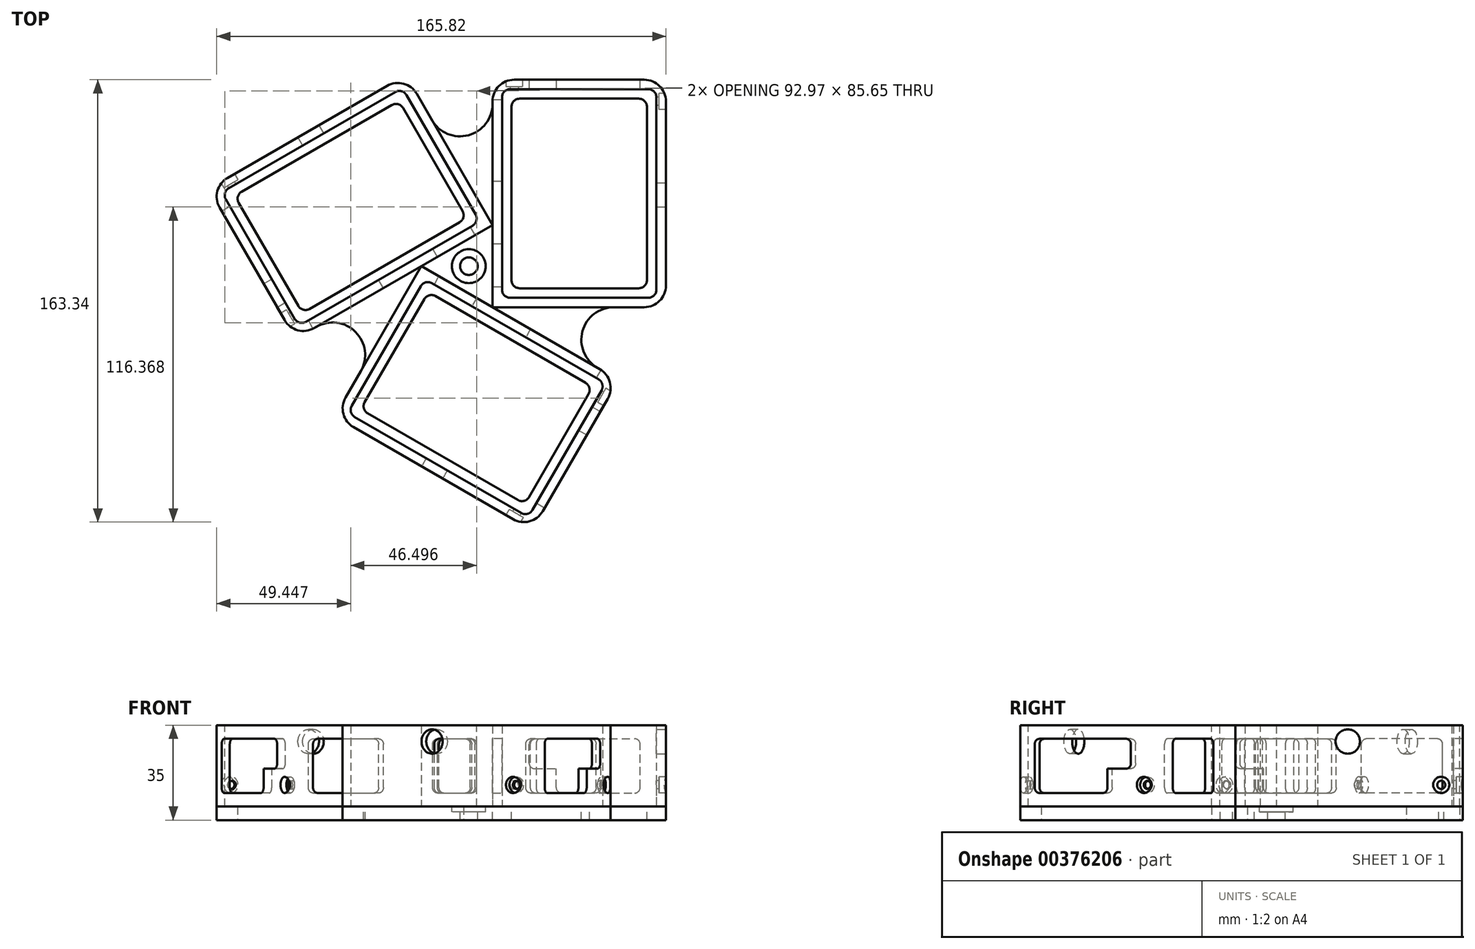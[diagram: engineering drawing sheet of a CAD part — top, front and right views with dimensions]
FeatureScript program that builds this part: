
annotation { "Feature Type Name" : "Feature", "Feature Type Description" : "" }
export const myFeature = defineFeature(function(context is Context, id is Id, definition is map)
    precondition{}
    {
        {
            var Q0;
            Q0=qCreatedBy(makeId("Top.planeOp"),FACE);
            var sketch = newSketch(context, id + "F0", { "sketchPlane" : qUnion([Q0])});
            skCircle(sketch, "E0.cCircle", {"center": v(0, 0) * mm, "radius": 8.75 * mm, "construction": true});
            skLineSegment(sketch, "E1.bottom", {"start": v(12.25, 65.34) * mm, "end": v(69.25, 65.34) * mm});
            skLineSegment(sketch, "E1.top", {"start": v(12.25, -11.66) * mm, "end": v(69.25, -11.66) * mm});
            skLineSegment(sketch, "E1.left", {"start": v(12.25, 65.34) * mm, "end": v(12.25, -11.66) * mm});
            skLineSegment(sketch, "E1.right", {"start": v(69.25, 65.34) * mm, "end": v(69.25, -11.66) * mm});
            skLineSegment(sketch, "E2.0", {"start": v(8.75, 68.84) * mm, "end": v(72.75, 68.84) * mm});
            skLineSegment(sketch, "E2.1", {"start": v(8.75, 68.84) * mm, "end": v(8.75, -15.16) * mm});
            skLineSegment(sketch, "E2.2", {"start": v(8.75, -15.16) * mm, "end": v(72.75, -15.16) * mm});
            skLineSegment(sketch, "E2.3", {"start": v(72.75, 68.84) * mm, "end": v(72.75, -15.16) * mm});
            skLineSegment(sketch, "E3.bottom", {"start": v(-44.72, -54.14) * mm, "end": v(-16.22, -4.78) * mm});
            skLineSegment(sketch, "E3.top", {"start": v(21.97, -92.64) * mm, "end": v(50.47, -43.28) * mm});
            skLineSegment(sketch, "E3.left", {"start": v(-44.72, -54.14) * mm, "end": v(21.97, -92.64) * mm});
            skLineSegment(sketch, "E3.right", {"start": v(-16.22, -4.78) * mm, "end": v(50.47, -43.28) * mm});
            skLineSegment(sketch, "E4.0", {"start": v(-49.5, -55.43) * mm, "end": v(-17.5, 0) * mm});
            skLineSegment(sketch, "E4.1", {"start": v(-49.5, -55.43) * mm, "end": v(23.25, -97.43) * mm});
            skLineSegment(sketch, "E4.2", {"start": v(23.25, -97.43) * mm, "end": v(55.25, -42) * mm});
            skLineSegment(sketch, "E4.3", {"start": v(-17.5, 0) * mm, "end": v(55.25, -42) * mm});
            skLineSegment(sketch, "E5.0", {"start": v(-64, -26.84) * mm, "end": v(-96, 28.58) * mm});
            skLineSegment(sketch, "E5.1", {"start": v(-64, -26.84) * mm, "end": v(8.75, 15.16) * mm});
            skLineSegment(sketch, "E5.2", {"start": v(8.75, 15.16) * mm, "end": v(-23.25, 70.58) * mm});
            skLineSegment(sketch, "E5.3", {"start": v(-96, 28.58) * mm, "end": v(-23.25, 70.58) * mm});
            skLineSegment(sketch, "E6.0", {"start": v(15.75, 61.84) * mm, "end": v(15.75, -8.16) * mm});
            skLineSegment(sketch, "E6.1", {"start": v(15.75, 61.84) * mm, "end": v(65.75, 61.84) * mm});
            skLineSegment(sketch, "E6.2", {"start": v(65.75, 61.84) * mm, "end": v(65.75, -8.16) * mm});
            skLineSegment(sketch, "E6.3", {"start": v(15.75, -8.16) * mm, "end": v(65.75, -8.16) * mm});
            skLineSegment(sketch, "E7.0", {"start": v(-39.94, -52.86) * mm, "end": v(-14.94, -9.56) * mm});
            skLineSegment(sketch, "E7.1", {"start": v(-39.94, -52.86) * mm, "end": v(20.68, -87.86) * mm});
            skLineSegment(sketch, "E7.2", {"start": v(20.68, -87.86) * mm, "end": v(45.68, -44.56) * mm});
            skLineSegment(sketch, "E7.3", {"start": v(-14.94, -9.56) * mm, "end": v(45.68, -44.56) * mm});
            skCircle(sketch, "E8", {"center": v(0, 0) * mm, "radius": 6.25 * mm});
            skCircle(sketch, "E9", {"center": v(0, 0) * mm, "radius": 3.25 * mm});
            skLineSegment(sketch, "E10.0", {"start": v(-91.22, 27.3) * mm, "end": v(-24.53, 65.8) * mm});
            skLineSegment(sketch, "E10.1", {"start": v(-62.72, -22.06) * mm, "end": v(-91.22, 27.3) * mm});
            skLineSegment(sketch, "E10.2", {"start": v(-62.72, -22.06) * mm, "end": v(3.97, 16.44) * mm});
            skLineSegment(sketch, "E10.3", {"start": v(3.97, 16.44) * mm, "end": v(-24.53, 65.8) * mm});
            skLineSegment(sketch, "E11.0", {"start": v(-86.43, 26.02) * mm, "end": v(-25.81, 61.02) * mm});
            skLineSegment(sketch, "E11.1", {"start": v(-61.43, -17.28) * mm, "end": v(-86.43, 26.02) * mm});
            skLineSegment(sketch, "E11.2", {"start": v(-61.43, -17.28) * mm, "end": v(-0.81, 17.72) * mm});
            skLineSegment(sketch, "E11.3", {"start": v(-0.81, 17.72) * mm, "end": v(-25.81, 61.02) * mm});
            skSolve(sketch);
        }
        {
            var Q0;
            Q0=makeQuery(id+"F0.imprint","IMPRINT",FACE,{"disambiguationData":[TD([[makeQuery(id+"F0.imprint","IMPRINT",EDGE,{"derivedFrom":sQuery(id+"F0.wireOp",EDGE,"E1.bottom")}),1.0]])]});
            var Q1;
            Q1=makeQuery(id+"F0.imprint","IMPRINT",FACE,{"disambiguationData":[TD([[makeQuery(id+"F0.imprint","IMPRINT",EDGE,{"derivedFrom":sQuery(id+"F0.wireOp",EDGE,"E1.bottom")}),-1.0]])]});
            var Q2;
            Q2=makeQuery(id+"F0.imprint","IMPRINT",FACE,{"disambiguationData":[TD([[makeQuery(id+"F0.imprint","IMPRINT",EDGE,{"derivedFrom":sQuery(id+"F0.wireOp",EDGE,"fd176c51-96d4-47cc-b5ac-51faa9285e0e.bottom")}),1.0]])]});
            var Q3;
            Q3=makeQuery(id+"F0.imprint","IMPRINT",FACE,{"disambiguationData":[TD([[makeQuery(id+"F0.imprint","IMPRINT",EDGE,{"derivedFrom":sQuery(id+"F0.wireOp",EDGE,"fd176c51-96d4-47cc-b5ac-51faa9285e0e.bottom")}),-1.0]])]});
            var Q4;
            {var subQ3=sQuery(id+"F0.wireOp",EDGE,"Trs6sdYQ-4i84-jObw-JwDY-IEx57dNpuPkq");Q4=makeQuery(id+"F0.imprint","IMPRINT",FACE,{"disambiguationData":[TD([[makeQuery(id+"F0.imprint","IMPRINT",EDGE,{"derivedFrom":subQ3}),1.0]])]});}
            var Q5;
            {var subQ3=sQuery(id+"F0.wireOp",EDGE,"4pj0R1mP-d1zE-uwOY-dOB5-XZU3ohouCTzi");Q5=makeQuery(id+"F0.imprint","IMPRINT",FACE,{"disambiguationData":[TD([[makeQuery(id+"F0.imprint","IMPRINT",EDGE,{"derivedFrom":subQ3}),1.0]])]});}
            var Q6;
            {var subQ0=sQuery(id+"F0.wireOp",EDGE,"E0.0");Q6=makeQuery(id+"F0.imprint","IMPRINT",FACE,{"disambiguationData":[TD([[makeQuery(id+"F0.imprint","IMPRINT",EDGE,{"derivedFrom":subQ0}),1.0]])]});}
            var Q7;
            {var subQ0=sQuery(id+"F0.wireOp",EDGE,"E5.2");Q7=makeQuery(id+"F0.imprint","IMPRINT",FACE,{"disambiguationData":[TD([[makeQuery(id+"F0.imprint","IMPRINT",EDGE,{"derivedFrom":subQ0}),-1.0]])]});}
            var Q8;
            {var subQ0=sQuery(id+"F0.wireOp",EDGE,"E2.2");Q8=makeQuery(id+"F0.imprint","IMPRINT",FACE,{"disambiguationData":[TD([[makeQuery(id+"F0.imprint","IMPRINT",EDGE,{"derivedFrom":subQ0}),-1.0]])]});}
            var Q9;
            {var subQ0=sQuery(id+"F0.wireOp",EDGE,"E0.0");Q9=makeQuery(id+"F0.imprint","IMPRINT",FACE,{"disambiguationData":[TD([[makeQuery(id+"F0.imprint","IMPRINT",EDGE,{"derivedFrom":subQ0}),-1.0]])]});}
            var Q10;
            Q10=makeQuery(id+"F0.imprint","IMPRINT",FACE,{"disambiguationData":[TD([[makeQuery(id+"F0.imprint","IMPRINT",EDGE,{"derivedFrom":sQuery(id+"F0.wireOp",EDGE,"E3.bottom")}),-1.0]])]});
            var Q11;
            Q11=makeQuery(id+"F0.imprint","IMPRINT",FACE,{"disambiguationData":[TD([[makeQuery(id+"F0.imprint","IMPRINT",EDGE,{"derivedFrom":sQuery(id+"F0.wireOp",EDGE,"E3.bottom")}),1.0]])]});
            var Q12;
            {var subQ3=sQuery(id+"F0.wireOp",EDGE,"SlVnMKC8-odKH-QQK0-Q7Xs-DCQOM6dgWicU");Q12=makeQuery(id+"F0.imprint","IMPRINT",FACE,{"disambiguationData":[TD([[makeQuery(id+"F0.imprint","IMPRINT",EDGE,{"derivedFrom":subQ3}),1.0]])]});}
            var Q13;
            Q13=makeQuery(id+"F0.imprint","IMPRINT",FACE,{"disambiguationData":[TD([[makeQuery(id+"F0.imprint","IMPRINT",EDGE,{"derivedFrom":sQuery(id+"F0.wireOp",EDGE,"E8")}),-1.0]])]});
            var Q14;
            Q14=makeQuery(id+"F0.imprint","IMPRINT",FACE,{"disambiguationData":[TD([[makeQuery(id+"F0.imprint","IMPRINT",EDGE,{"derivedFrom":sQuery(id+"F0.wireOp",EDGE,"E8")}),1.0]])]});
            var Q15;
            {var subQ5=sQuery(id+"F0.wireOp",EDGE,"E5.0");Q15=makeQuery(id+"F0.imprint","IMPRINT",FACE,{"disambiguationData":[TD([[makeQuery(id+"F0.imprint","IMPRINT",EDGE,{"derivedFrom":subQ5}),-1.0]])]});}
            var Q16;
            Q16=makeQuery(id+"F0.imprint","IMPRINT",FACE,{"disambiguationData":[TD([[makeQuery(id+"F0.imprint","IMPRINT",EDGE,{"derivedFrom":sQuery(id+"F0.wireOp",EDGE,"E10.0")}),-1.0]])]});
            extrude(context, id + "F1", {"entities" : qUnion([Q0, Q1, Q2, Q3, Q4, Q5, Q6, Q7, Q8, Q9, Q10, Q11, Q12, Q13, Q14, Q15, Q16]), "oppositeDirection" : true, "depth" : 5 * mm, "offsetDistance" : 25 * mm});
        }
        {
            var Q0;
            Q0=makeQuery(id+"F0.imprint","IMPRINT",FACE,{"disambiguationData":[TD([[makeQuery(id+"F0.imprint","IMPRINT",EDGE,{"derivedFrom":sQuery(id+"F0.wireOp",EDGE,"E8")}),1.0]])]});
            extrude(context, id + "F2", {"entities" : qUnion([Q0]), "operationType" : NewBodyOperationType.REMOVE, "oppositeDirection" : true, "depth" : 2 * mm, "offsetDistance" : 25 * mm});
        }
        {
            var Q0;
            Q0=makeQuery(id+"F0.imprint","IMPRINT",FACE,{"disambiguationData":[TD([[makeQuery(id+"F0.imprint","IMPRINT",EDGE,{"derivedFrom":sQuery(id+"F0.wireOp",EDGE,"E1.bottom")}),-1.0]])]});
            var Q1;
            Q1=makeQuery(id+"F0.imprint","IMPRINT",FACE,{"disambiguationData":[TD([[makeQuery(id+"F0.imprint","IMPRINT",EDGE,{"derivedFrom":sQuery(id+"F0.wireOp",EDGE,"fd176c51-96d4-47cc-b5ac-51faa9285e0e.bottom")}),-1.0]])]});
            var Q2;
            Q2=makeQuery(id+"F0.imprint","IMPRINT",FACE,{"disambiguationData":[TD([[makeQuery(id+"F0.imprint","IMPRINT",EDGE,{"derivedFrom":sQuery(id+"F0.wireOp",EDGE,"E3.bottom")}),-1.0]])]});
            extrude(context, id + "F3", {"entities" : qUnion([Q0, Q1, Q2]), "operationType" : NewBodyOperationType.REMOVE, "depth" : 3 * mm, "offsetDistance" : 25 * mm});
        }
        {
            var Q0;
            Q0=makeQuery(id+"F0.imprint","IMPRINT",FACE,{"disambiguationData":[TD([[makeQuery(id+"F0.imprint","IMPRINT",EDGE,{"derivedFrom":sQuery(id+"F0.wireOp",EDGE,"E1.bottom")}),1.0]])]});
            var Q1;
            Q1=makeQuery(id+"F0.imprint","IMPRINT",FACE,{"disambiguationData":[TD([[makeQuery(id+"F0.imprint","IMPRINT",EDGE,{"derivedFrom":sQuery(id+"F0.wireOp",EDGE,"E3.bottom")}),1.0]])]});
            var Q2;
            Q2=makeQuery(id+"F0.imprint","IMPRINT",FACE,{"disambiguationData":[TD([[makeQuery(id+"F0.imprint","IMPRINT",EDGE,{"derivedFrom":sQuery(id+"F0.wireOp",EDGE,"fd176c51-96d4-47cc-b5ac-51faa9285e0e.bottom")}),1.0]])]});
            var Q3;
            {var subQ5=sQuery(id+"F0.wireOp",EDGE,"E5.0");Q3=makeQuery(id+"F0.imprint","IMPRINT",FACE,{"disambiguationData":[TD([[makeQuery(id+"F0.imprint","IMPRINT",EDGE,{"derivedFrom":subQ5}),-1.0]])]});}
            extrude(context, id + "F4", {"entities" : qUnion([Q0, Q1, Q2, Q3]), "depth" : 30 * mm, "offsetDistance" : 25 * mm});
        }
        {
            var Q0;
            Q0=makeQuery(id+"F4.opExtrude","CAP_FACE",FACE,{"disambiguationData":[OSD([sQuery(id+"F0.wireOp",EDGE,"fd176c51-96d4-47cc-b5ac-51faa9285e0e.bottom"),sQuery(id+"F0.wireOp",EDGE,"fd176c51-96d4-47cc-b5ac-51faa9285e0e.top"),sQuery(id+"F0.wireOp",EDGE,"fd176c51-96d4-47cc-b5ac-51faa9285e0e.left"),sQuery(id+"F0.wireOp",EDGE,"fd176c51-96d4-47cc-b5ac-51faa9285e0e.right"),sQuery(id+"F0.wireOp",EDGE,"E5.0"),sQuery(id+"F0.wireOp",EDGE,"E5.1"),sQuery(id+"F0.wireOp",EDGE,"E5.2"),sQuery(id+"F0.wireOp",EDGE,"E5.3")])],"isStart":false});
            var sketch = newSketch(context, id + "F5", { "sketchPlane" : qUnion([Q0])});
            skLineSegment(sketch, "E12", {"start": v(-91.25, 20.35) * mm, "end": v(-88.22, 22.1) * mm});
            skLineSegment(sketch, "E13", {"start": v(-88.22, 22.1) * mm, "end": v(-72.72, -4.74) * mm});
            skLineSegment(sketch, "E14", {"start": v(-72.72, -4.74) * mm, "end": v(-75.75, -6.5) * mm});
            skLineSegment(sketch, "E15", {"start": v(-75.75, -6.5) * mm, "end": v(-91.25, 20.35) * mm});
            skLineSegment(sketch, "E16", {"start": v(-75.75, -6.5) * mm, "end": v(-70.75, -15.15) * mm});
            skLineSegment(sketch, "E17", {"start": v(-70.75, -15.15) * mm, "end": v(-67.72, -13.4) * mm});
            skLineSegment(sketch, "E18", {"start": v(-67.72, -13.4) * mm, "end": v(-72.72, -4.74) * mm});
            skLineSegment(sketch, "E19", {"start": v(-59.25, -20.06) * mm, "end": v(-57.5, -23.1) * mm});
            skLineSegment(sketch, "E20", {"start": v(-57.5, -23.1) * mm, "end": v(-31.52, -8.1) * mm});
            skLineSegment(sketch, "E21", {"start": v(-31.52, -8.1) * mm, "end": v(-33.27, -5.06) * mm});
            skLineSegment(sketch, "E22", {"start": v(-33.27, -5.06) * mm, "end": v(-59.25, -20.06) * mm});
            skLineSegment(sketch, "E23", {"start": v(-11.6, 3.4) * mm, "end": v(-13.35, 6.44) * mm});
            skLineSegment(sketch, "E24", {"start": v(-13.35, 6.44) * mm, "end": v(0.5, 14.44) * mm});
            skLineSegment(sketch, "E25", {"start": v(0.5, 14.44) * mm, "end": v(2.25, 11.4) * mm});
            skLineSegment(sketch, "E26", {"start": v(2.25, 11.4) * mm, "end": v(-11.6, 3.4) * mm});
            skSolve(sketch);
        }
        {
            var Q0;
            Q0=makeQuery(id+"F4.opExtrude","CAP_FACE",FACE,{"disambiguationData":[OSD([sQuery(id+"F0.wireOp",EDGE,"E3.bottom"),sQuery(id+"F0.wireOp",EDGE,"E3.top"),sQuery(id+"F0.wireOp",EDGE,"E3.left"),sQuery(id+"F0.wireOp",EDGE,"E3.right"),sQuery(id+"F0.wireOp",EDGE,"E4.0"),sQuery(id+"F0.wireOp",EDGE,"E4.1"),sQuery(id+"F0.wireOp",EDGE,"E4.2"),sQuery(id+"F0.wireOp",EDGE,"E4.3")])],"isStart":false});
            var sketch = newSketch(context, id + "F6", { "sketchPlane" : qUnion([Q0])});
            skLineSegment(sketch, "E27", {"start": v(24.97, -87.45) * mm, "end": v(28, -89.2) * mm});
            skLineSegment(sketch, "E28", {"start": v(28, -89.2) * mm, "end": v(43.5, -62.35) * mm});
            skLineSegment(sketch, "E29", {"start": v(43.5, -62.35) * mm, "end": v(40.47, -60.6) * mm});
            skLineSegment(sketch, "E30", {"start": v(40.47, -60.6) * mm, "end": v(24.97, -87.45) * mm});
            skLineSegment(sketch, "E31", {"start": v(40.47, -60.6) * mm, "end": v(45.47, -51.94) * mm});
            skLineSegment(sketch, "E32", {"start": v(45.47, -51.94) * mm, "end": v(48.5, -53.7) * mm});
            skLineSegment(sketch, "E33", {"start": v(48.5, -53.7) * mm, "end": v(43.5, -62.35) * mm});
            skLineSegment(sketch, "E34", {"start": v(48.75, -38.25) * mm, "end": v(22.77, -23.25) * mm});
            skLineSegment(sketch, "E35", {"start": v(48.75, -38.25) * mm, "end": v(47, -41.28) * mm});
            skLineSegment(sketch, "E36", {"start": v(22.77, -23.25) * mm, "end": v(21.02, -26.28) * mm});
            skLineSegment(sketch, "E37", {"start": v(21.02, -26.28) * mm, "end": v(47, -41.28) * mm});
            skLineSegment(sketch, "E38", {"start": v(-12.75, -6.78) * mm, "end": v(-11, -3.75) * mm});
            skLineSegment(sketch, "E39", {"start": v(-11, -3.75) * mm, "end": v(2.85, -11.75) * mm});
            skLineSegment(sketch, "E40", {"start": v(2.85, -11.75) * mm, "end": v(1.1, -14.78) * mm});
            skLineSegment(sketch, "E41", {"start": v(1.1, -14.78) * mm, "end": v(-12.75, -6.78) * mm});
            skSolve(sketch);
        }
        {
            var Q0;
            Q0=makeQuery(id+"F4.opExtrude","CAP_FACE",FACE,{"disambiguationData":[OSD([sQuery(id+"F0.wireOp",EDGE,"E1.bottom"),sQuery(id+"F0.wireOp",EDGE,"E1.top"),sQuery(id+"F0.wireOp",EDGE,"E1.left"),sQuery(id+"F0.wireOp",EDGE,"E1.right"),sQuery(id+"F0.wireOp",EDGE,"E2.0"),sQuery(id+"F0.wireOp",EDGE,"E2.1"),sQuery(id+"F0.wireOp",EDGE,"E2.2"),sQuery(id+"F0.wireOp",EDGE,"E2.3")])],"isStart":false});
            var sketch = newSketch(context, id + "F7", { "sketchPlane" : qUnion([Q0])});
            skLineSegment(sketch, "E42", {"start": v(32.25, 68.84) * mm, "end": v(32.25, 65.34) * mm});
            skLineSegment(sketch, "E43", {"start": v(32.25, 65.34) * mm, "end": v(63.25, 65.34) * mm});
            skLineSegment(sketch, "E44", {"start": v(63.25, 65.34) * mm, "end": v(63.25, 68.84) * mm});
            skLineSegment(sketch, "E45", {"start": v(63.25, 68.84) * mm, "end": v(32.25, 68.84) * mm});
            skLineSegment(sketch, "E46", {"start": v(32.25, 68.84) * mm, "end": v(22.25, 68.84) * mm});
            skLineSegment(sketch, "E47", {"start": v(22.25, 68.84) * mm, "end": v(22.25, 65.34) * mm});
            skLineSegment(sketch, "E48", {"start": v(22.25, 65.34) * mm, "end": v(32.25, 65.34) * mm});
            skLineSegment(sketch, "E49", {"start": v(12.25, 61.34) * mm, "end": v(8.75, 61.34) * mm});
            skLineSegment(sketch, "E50", {"start": v(12.25, 31.34) * mm, "end": v(12.25, 61.34) * mm});
            skLineSegment(sketch, "E51", {"start": v(12.25, 31.34) * mm, "end": v(8.75, 31.34) * mm});
            skLineSegment(sketch, "E52", {"start": v(8.75, 31.34) * mm, "end": v(8.75, 61.34) * mm});
            skLineSegment(sketch, "E53", {"start": v(8.75, 8.34) * mm, "end": v(12.25, 8.34) * mm});
            skLineSegment(sketch, "E54", {"start": v(12.25, 8.34) * mm, "end": v(12.25, -7.66) * mm});
            skLineSegment(sketch, "E55", {"start": v(12.25, -7.66) * mm, "end": v(8.75, -7.66) * mm});
            skLineSegment(sketch, "E56", {"start": v(8.75, -7.66) * mm, "end": v(8.75, 8.34) * mm});
            skSolve(sketch);
        }
        {
            var Q0;
            Q0=makeQuery(id+"F6.imprint","IMPRINT",FACE,{"disambiguationData":[TD([[makeQuery(id+"F6.imprint","IMPRINT",EDGE,{"derivedFrom":sQuery(id+"F6.wireOp",EDGE,"E27")}),1.0]])]});
            var Q1;
            Q1=makeQuery(id+"F7.imprint","IMPRINT",FACE,{"disambiguationData":[TD([[makeQuery(id+"F7.imprint","IMPRINT",EDGE,{"derivedFrom":sQuery(id+"F7.wireOp",EDGE,"E42")}),1.0]])]});
            var Q2;
            Q2=makeQuery(id+"F5.imprint","IMPRINT",FACE,{"disambiguationData":[TD([[makeQuery(id+"F5.imprint","IMPRINT",EDGE,{"derivedFrom":sQuery(id+"F5.wireOp",EDGE,"E12")}),-1.0]])]});
            var Q3;
            Q3=makeQuery(id+"F5.imprint","IMPRINT",FACE,{"disambiguationData":[TD([[makeQuery(id+"F5.imprint","IMPRINT",EDGE,{"derivedFrom":sQuery(id+"F5.wireOp",EDGE,"E19")}),1.0]])]});
            var Q4;
            Q4=makeQuery(id+"F7.imprint","IMPRINT",FACE,{"disambiguationData":[TD([[makeQuery(id+"F7.imprint","IMPRINT",EDGE,{"derivedFrom":sQuery(id+"F7.wireOp",EDGE,"E49")}),1.0]])]});
            var Q5;
            Q5=makeQuery(id+"F6.imprint","IMPRINT",FACE,{"disambiguationData":[TD([[makeQuery(id+"F6.imprint","IMPRINT",EDGE,{"derivedFrom":sQuery(id+"F6.wireOp",EDGE,"E34")}),-1.0]])]});
            var Q6;
            Q6=makeQuery(id+"F7.imprint","IMPRINT",FACE,{"disambiguationData":[TD([[makeQuery(id+"F7.imprint","IMPRINT",EDGE,{"derivedFrom":sQuery(id+"F7.wireOp",EDGE,"E53")}),-1.0]])]});
            var Q7;
            Q7=makeQuery(id+"F5.imprint","IMPRINT",FACE,{"disambiguationData":[TD([[makeQuery(id+"F5.imprint","IMPRINT",EDGE,{"derivedFrom":sQuery(id+"F5.wireOp",EDGE,"E23")}),-1.0]])]});
            var Q8;
            Q8=makeQuery(id+"F6.imprint","IMPRINT",FACE,{"disambiguationData":[TD([[makeQuery(id+"F6.imprint","IMPRINT",EDGE,{"derivedFrom":sQuery(id+"F6.wireOp",EDGE,"E38")}),-1.0]])]});
            extrude(context, id + "F8", {"entities" : qUnion([Q0, Q1, Q2, Q3, Q4, Q5, Q6, Q7, Q8]), "operationType" : NewBodyOperationType.REMOVE, "oppositeDirection" : true, "depth" : 25 * mm, "offsetDistance" : 25 * mm, "hasSecondDirection" : true, "secondDirectionOppositeDirection" : true, "secondDirectionDepth" : 5 * mm});
        }
        {
            var Q0;
            Q0=makeQuery(id+"F5.imprint","IMPRINT",FACE,{"disambiguationData":[TD([[makeQuery(id+"F5.imprint","IMPRINT",EDGE,{"derivedFrom":sQuery(id+"F5.wireOp",EDGE,"E14")}),1.0]])]});
            var Q1;
            Q1=makeQuery(id+"F6.imprint","IMPRINT",FACE,{"disambiguationData":[TD([[makeQuery(id+"F6.imprint","IMPRINT",EDGE,{"derivedFrom":sQuery(id+"F6.wireOp",EDGE,"E29")}),-1.0]])]});
            var Q2;
            Q2=makeQuery(id+"F7.imprint","IMPRINT",FACE,{"disambiguationData":[TD([[makeQuery(id+"F7.imprint","IMPRINT",EDGE,{"derivedFrom":sQuery(id+"F7.wireOp",EDGE,"E42")}),-1.0]])]});
            extrude(context, id + "F9", {"entities" : qUnion([Q0, Q1, Q2]), "operationType" : NewBodyOperationType.REMOVE, "oppositeDirection" : true, "depth" : 16 * mm, "offsetDistance" : 25 * mm, "hasSecondDirection" : true, "secondDirectionOppositeDirection" : true, "secondDirectionDepth" : 5 * mm});
        }
        {
            var Q0;
            Q0=makeQuery(id+"F4.opExtrude","SWEPT_FACE",FACE,{"disambiguationData":[OSD([sQuery(id+"F0.wireOp",EDGE,"E4.1")])]});
            var sketch = newSketch(context, id + "F10", { "sketchPlane" : qUnion([Q0])});
            skCircle(sketch, "E57", {"center": v(26.34, 24) * mm, "radius": 4.5 * mm});
            skSolve(sketch);
        }
        {
            var Q0;
            Q0=makeQuery(id+"F4.opExtrude","SWEPT_FACE",FACE,{"disambiguationData":[OSD([sQuery(id+"F0.wireOp",EDGE,"E2.3")])]});
            var sketch = newSketch(context, id + "F11", { "sketchPlane" : qUnion([Q0])});
            skCircle(sketch, "E58", {"center": v(26.34, 24) * mm, "radius": 4.5 * mm});
            skSolve(sketch);
        }
        {
            var Q0;
            Q0=makeQuery(id+"F4.opExtrude","SWEPT_FACE",FACE,{"disambiguationData":[OSD([sQuery(id+"F0.wireOp",EDGE,"E5.3")])]});
            var sketch = newSketch(context, id + "F12", { "sketchPlane" : qUnion([Q0])});
            skCircle(sketch, "E59", {"center": v(26.34, 24) * mm, "radius": 4.5 * mm});
            skSolve(sketch);
        }
        {
            var Q0;
            Q0=qSketchRegion(id+"F10",true);
            extrude(context, id + "F13", {"entities" : qUnion([Q0]), "operationType" : NewBodyOperationType.REMOVE, "oppositeDirection" : true, "depth" : 25 * mm, "offsetDistance" : 25 * mm});
        }
        {
            var Q0;
            Q0=makeQuery(id+"F12.imprint","IMPRINT",FACE,{"disambiguationData":[TD([[makeQuery(id+"F12.imprint","IMPRINT",EDGE,{"derivedFrom":sQuery(id+"F12.wireOp",EDGE,"E59")}),1.0]])]});
            extrude(context, id + "F14", {"entities" : qUnion([Q0]), "operationType" : NewBodyOperationType.REMOVE, "oppositeDirection" : true, "depth" : 25 * mm, "offsetDistance" : 25 * mm});
        }
        {
            var Q0;
            Q0=makeQuery(id+"F11.imprint","IMPRINT",FACE,{"disambiguationData":[TD([[makeQuery(id+"F11.imprint","IMPRINT",EDGE,{"derivedFrom":sQuery(id+"F11.wireOp",EDGE,"E58")}),1.0]])]});
            extrude(context, id + "F15", {"entities" : qUnion([Q0]), "operationType" : NewBodyOperationType.REMOVE, "oppositeDirection" : true, "depth" : 25 * mm, "offsetDistance" : 25 * mm});
        }
        {
            var Q0;
            Q0=makeQuery(id+"F4.opExtrude","SWEPT_FACE",FACE,{"disambiguationData":[OSD([sQuery(id+"F0.wireOp",EDGE,"E5.0")])]});
            var sketch = newSketch(context, id + "F16", { "sketchPlane" : qUnion([Q0])});
            skSolve(sketch);
        }
        {
            var Q0;
            Q0=makeQuery(id+"F10.imprint","IMPRINT",FACE,{"disambiguationData":[TD([[makeQuery(id+"F10.imprint","IMPRINT",EDGE,{"derivedFrom":sQuery(id+"F10.wireOp",EDGE,"E57")}),-1.0]])]});
            var sketch = newSketch(context, id + "F17", { "sketchPlane" : qUnion([Q0])});
            skCircle(sketch, "E60", {"center": v(60.84, 8) * mm, "radius": 6.85 * mm});
            skSolve(sketch);
        }
        {
            var Q0;
            Q0=makeQuery(id+"F4.opExtrude","SWEPT_FACE",FACE,{"disambiguationData":[OSD([sQuery(id+"F0.wireOp",EDGE,"E4.2")])]});
            var sketch = newSketch(context, id + "F18", { "sketchPlane" : qUnion([Q0])});
            skCircle(sketch, "E61", {"center": v(-16.75, 8) * mm, "radius": 11.71 * mm});
            skSolve(sketch);
        }
        {
            var Q0;
            Q0=makeQuery(id+"F11.imprint","IMPRINT",FACE,{"disambiguationData":[TD([[makeQuery(id+"F11.imprint","IMPRINT",EDGE,{"derivedFrom":sQuery(id+"F11.wireOp",EDGE,"E58")}),-1.0]])]});
            var sketch = newSketch(context, id + "F19", { "sketchPlane" : qUnion([Q0])});
            skCircle(sketch, "E62", {"center": v(60.84, 8) * mm, "radius": 5.05 * mm});
            skSolve(sketch);
        }
        {
            var Q0;
            Q0=makeQuery(id+"F4.opExtrude","SWEPT_FACE",FACE,{"disambiguationData":[OSD([sQuery(id+"F0.wireOp",EDGE,"E2.0")])]});
            var sketch = newSketch(context, id + "F20", { "sketchPlane" : qUnion([Q0])});
            skCircle(sketch, "E63", {"center": v(-16.75, 8) * mm, "radius": 7.5 * mm});
            skSolve(sketch);
        }
        {
            var Q0;
            Q0=makeQuery(id+"F12.imprint","IMPRINT",FACE,{"disambiguationData":[TD([[makeQuery(id+"F12.imprint","IMPRINT",EDGE,{"derivedFrom":sQuery(id+"F12.wireOp",EDGE,"E59")}),-1.0]])]});
            var sketch = newSketch(context, id + "F21", { "sketchPlane" : qUnion([Q0])});
            skCircle(sketch, "E64", {"center": v(60.84, 8) * mm, "radius": 3.21 * mm});
            skSolve(sketch);
        }
        {
            var Q0;
            {var subQ0=sQuery(id+"F0.wireOp",EDGE,"E5.0");Q0=makeQuery(id+"F16.imprint","IMPRINT",FACE,{"disambiguationData":[TD([[makeQuery(id+"F16.imprint","IMPRINT",EDGE,{"derivedFrom":makeQuery(id+"F4.opExtrude","CAP_EDGE",EDGE,{"disambiguationData":[OSD([subQ0])],"isStart":true})}),-1.0]])]});}
            var sketch = newSketch(context, id + "F22", { "sketchPlane" : qUnion([Q0])});
            skCircle(sketch, "E65", {"center": v(-16.75, 8) * mm, "radius": 8.32 * mm});
            skSolve(sketch);
        }
        {
            var Q0;
            Q0=sQuery(id+"F22.wireOp",VERTEX,"E65.center");
            var Q1;
            Q1=sQuery(id+"F21.wireOp",VERTEX,"E64.center");
            var Q2;
            Q2=sQuery(id+"F20.wireOp",VERTEX,"E63.center");
            var Q3;
            Q3=sQuery(id+"F19.wireOp",VERTEX,"E62.center");
            var Q4;
            Q4=sQuery(id+"F18.wireOp",VERTEX,"E61.center");
            var Q5;
            Q5=sQuery(id+"F17.wireOp",VERTEX,"E60.center");
            var Q6;
            Q6=makeQuery(id+"F4.opExtrude","SWEPT_BODY",BODY,{"disambiguationData":[OSD([sQuery(id+"F0.wireOp",EDGE,"E1.bottom"),sQuery(id+"F0.wireOp",EDGE,"E1.top"),sQuery(id+"F0.wireOp",EDGE,"E1.left"),sQuery(id+"F0.wireOp",EDGE,"E1.right"),sQuery(id+"F0.wireOp",EDGE,"E2.0"),sQuery(id+"F0.wireOp",EDGE,"E2.1"),sQuery(id+"F0.wireOp",EDGE,"E2.2"),sQuery(id+"F0.wireOp",EDGE,"E2.3")])]});
            var Q7;
            Q7=makeQuery(id+"F4.opExtrude","SWEPT_BODY",BODY,{"disambiguationData":[OSD([sQuery(id+"F0.wireOp",EDGE,"E3.bottom"),sQuery(id+"F0.wireOp",EDGE,"E3.top"),sQuery(id+"F0.wireOp",EDGE,"E3.left"),sQuery(id+"F0.wireOp",EDGE,"E3.right"),sQuery(id+"F0.wireOp",EDGE,"E4.0"),sQuery(id+"F0.wireOp",EDGE,"E4.1"),sQuery(id+"F0.wireOp",EDGE,"E4.2"),sQuery(id+"F0.wireOp",EDGE,"E4.3")])]});
            var Q8;
            Q8=makeQuery(id+"F4.opExtrude","SWEPT_BODY",BODY,{"disambiguationData":[OSD([sQuery(id+"F0.wireOp",EDGE,"fd176c51-96d4-47cc-b5ac-51faa9285e0e.bottom"),sQuery(id+"F0.wireOp",EDGE,"fd176c51-96d4-47cc-b5ac-51faa9285e0e.top"),sQuery(id+"F0.wireOp",EDGE,"fd176c51-96d4-47cc-b5ac-51faa9285e0e.left"),sQuery(id+"F0.wireOp",EDGE,"fd176c51-96d4-47cc-b5ac-51faa9285e0e.right"),sQuery(id+"F0.wireOp",EDGE,"E5.0"),sQuery(id+"F0.wireOp",EDGE,"E5.1"),sQuery(id+"F0.wireOp",EDGE,"E5.2"),sQuery(id+"F0.wireOp",EDGE,"E5.3")])]});
            hole(context, id + "F23", {"style" : HoleStyle.C_BORE, "endStyle" : HoleEndStyle.BLIND, "holeDiameter" : 3 * mm, "cBoreDiameter" : 6 * mm, "cBoreDepth" : 2.5 * mm, "holeDepth" : 12 * mm, "isTappedThrough" : true, "tappedDepth" : 12 * mm, "tapClearance" : 3, "locations" : qUnion([Q0, Q1, Q2, Q3, Q4, Q5]), "scope" : qUnion([Q6, Q7, Q8])});
        }
        {
            var Q0;
            Q0=makeQuery(id+"F4.opExtrude","SWEPT_EDGE",EDGE,{"disambiguationData":[OSD([sQuery(id+"F0.wireOp",EDGE,"E2.0"),sQuery(id+"F0.wireOp",EDGE,"E2.3")])]});
            var Q1;
            Q1=makeQuery(id+"F1.opExtrude","SWEPT_EDGE",EDGE,{"disambiguationData":[OSD([sQuery(id+"F0.wireOp",EDGE,"E2.0"),sQuery(id+"F0.wireOp",EDGE,"E2.3")])]});
            var Q2;
            Q2=makeQuery(id+"F4.opExtrude","SWEPT_EDGE",EDGE,{"disambiguationData":[OSD([sQuery(id+"F0.wireOp",EDGE,"E2.0"),sQuery(id+"F0.wireOp",EDGE,"E2.1")])]});
            var Q3;
            Q3=makeQuery(id+"F4.opExtrude","SWEPT_EDGE",EDGE,{"disambiguationData":[OSD([sQuery(id+"F0.wireOp",EDGE,"E5.2"),sQuery(id+"F0.wireOp",EDGE,"E5.3")])]});
            var Q4;
            Q4=makeQuery(id+"F4.opExtrude","SWEPT_EDGE",EDGE,{"disambiguationData":[OSD([sQuery(id+"F0.wireOp",EDGE,"E5.0"),sQuery(id+"F0.wireOp",EDGE,"E5.3")])]});
            var Q5;
            Q5=makeQuery(id+"F1.opExtrude","SWEPT_EDGE",EDGE,{"disambiguationData":[OSD([sQuery(id+"F0.wireOp",EDGE,"E5.0"),sQuery(id+"F0.wireOp",EDGE,"E5.3")])]});
            var Q6;
            Q6=makeQuery(id+"F4.opExtrude","SWEPT_EDGE",EDGE,{"disambiguationData":[OSD([sQuery(id+"F0.wireOp",EDGE,"E5.0"),sQuery(id+"F0.wireOp",EDGE,"E5.1")])]});
            var Q7;
            Q7=makeQuery(id+"F4.opExtrude","SWEPT_EDGE",EDGE,{"disambiguationData":[OSD([sQuery(id+"F0.wireOp",EDGE,"E4.0"),sQuery(id+"F0.wireOp",EDGE,"E4.1")])]});
            var Q8;
            Q8=makeQuery(id+"F1.opExtrude","SWEPT_EDGE",EDGE,{"disambiguationData":[OSD([sQuery(id+"F0.wireOp",EDGE,"E4.1"),sQuery(id+"F0.wireOp",EDGE,"E4.2")])]});
            var Q9;
            Q9=makeQuery(id+"F4.opExtrude","SWEPT_EDGE",EDGE,{"disambiguationData":[OSD([sQuery(id+"F0.wireOp",EDGE,"E4.1"),sQuery(id+"F0.wireOp",EDGE,"E4.2")])]});
            var Q10;
            Q10=makeQuery(id+"F4.opExtrude","SWEPT_EDGE",EDGE,{"disambiguationData":[OSD([sQuery(id+"F0.wireOp",EDGE,"E2.2"),sQuery(id+"F0.wireOp",EDGE,"E2.3")])]});
            var Q11;
            Q11=makeQuery(id+"F4.opExtrude","SWEPT_EDGE",EDGE,{"disambiguationData":[OSD([sQuery(id+"F0.wireOp",EDGE,"E4.2"),sQuery(id+"F0.wireOp",EDGE,"E4.3"),sQuery(id+"F0.wireOp",EDGE,"GvQxyZa6-xjYC-LB9P-KkNv-2Mbj6IE8QspT")])]});
            var Q12;
            Q12=makeQuery(id+"F1.opExtrude","SWEPT_EDGE",EDGE,{"disambiguationData":[OSD([sQuery(id+"F0.wireOp",EDGE,"E5.0"),sQuery(id+"F0.wireOp",EDGE,"E5.1"),sQuery(id+"F0.wireOp",EDGE,"43ANLG2u-DkbN-IqXG-IHAb-kBjCn0TTmeMn")])]});
            var Q13;
            Q13=makeQuery(id+"F1.opExtrude","SWEPT_EDGE",EDGE,{"disambiguationData":[OSD([sQuery(id+"F0.wireOp",EDGE,"E4.0"),sQuery(id+"F0.wireOp",EDGE,"E4.1"),sQuery(id+"F0.wireOp",EDGE,"43ANLG2u-DkbN-IqXG-IHAb-kBjCn0TTmeMn")])]});
            var Q14;
            Q14=makeQuery(id+"F1.opExtrude","SWEPT_EDGE",EDGE,{"disambiguationData":[OSD([sQuery(id+"F0.wireOp",EDGE,"E4.2"),sQuery(id+"F0.wireOp",EDGE,"E4.3"),sQuery(id+"F0.wireOp",EDGE,"GvQxyZa6-xjYC-LB9P-KkNv-2Mbj6IE8QspT")])]});
            var Q15;
            Q15=makeQuery(id+"F1.opExtrude","SWEPT_EDGE",EDGE,{"disambiguationData":[OSD([sQuery(id+"F0.wireOp",EDGE,"E2.2"),sQuery(id+"F0.wireOp",EDGE,"E2.3"),sQuery(id+"F0.wireOp",EDGE,"GvQxyZa6-xjYC-LB9P-KkNv-2Mbj6IE8QspT")])]});
            var Q16;
            Q16=makeQuery(id+"F1.opExtrude","SWEPT_EDGE",EDGE,{"disambiguationData":[OSD([sQuery(id+"F0.wireOp",EDGE,"E2.0"),sQuery(id+"F0.wireOp",EDGE,"E2.1"),sQuery(id+"F0.wireOp",EDGE,"AugCb2wg-pMNL-8kHY-jx69-0p9t7WPqScGK")])]});
            var Q17;
            Q17=makeQuery(id+"F1.opExtrude","SWEPT_EDGE",EDGE,{"disambiguationData":[OSD([sQuery(id+"F0.wireOp",EDGE,"E5.2"),sQuery(id+"F0.wireOp",EDGE,"E5.3"),sQuery(id+"F0.wireOp",EDGE,"AugCb2wg-pMNL-8kHY-jx69-0p9t7WPqScGK")])]});
            var Q18;
            Q18=makeQuery(id+"F1.opExtrude","SWEPT_EDGE",EDGE,{"disambiguationData":[OSD([sQuery(id+"F0.wireOp",EDGE,"E4.0"),sQuery(id+"F0.wireOp",EDGE,"SlVnMKC8-odKH-QQK0-Q7Xs-DCQOM6dgWicU")])]});
            var Q19;
            Q19=makeQuery(id+"F1.opExtrude","SWEPT_EDGE",EDGE,{"disambiguationData":[OSD([sQuery(id+"F0.wireOp",EDGE,"E2.2"),sQuery(id+"F0.wireOp",EDGE,"nHmlda82-zJrG-7BgD-NYJj-D6Yqii4C212E")])]});
            var Q20;
            Q20=makeQuery(id+"F1.opExtrude","SWEPT_EDGE",EDGE,{"disambiguationData":[OSD([sQuery(id+"F0.wireOp",EDGE,"E5.2"),sQuery(id+"F0.wireOp",EDGE,"4Qk8wPaZ-tdU4-9A6E-ItYS-yzHQE8pdWD9T")])]});
            fillet(context, id + "F24", {"entities" : qUnion([Q0, Q1, Q2, Q3, Q4, Q5, Q6, Q7, Q8, Q9, Q10, Q11, Q12, Q13, Q14, Q15, Q16, Q17, Q18, Q19, Q20]), "radius" : 8 * mm, "tangentPropagation" : true, "allowEdgeOverflow" : false});
        }
        {
            var Q0;
            {var subQ0=sQuery(id+"F0.wireOp",EDGE,"E4.3");var subQ1=sQuery(id+"F0.wireOp",EDGE,"E4.2");var subQ2=sQuery(id+"F0.wireOp",EDGE,"E3.right");var subQ3=sQuery(id+"F0.wireOp",EDGE,"E3.top");Q0=makeQuery(id+"F8.boolean.opBoolean","SPLIT",EDGE,{"disambiguationData":[TD([makeQuery(id+"F4.opExtrude","CAP_FACE",FACE,{"disambiguationData":[OSD([sQuery(id+"F0.wireOp",EDGE,"E3.bottom"),subQ3,sQuery(id+"F0.wireOp",EDGE,"E3.left"),subQ2,sQuery(id+"F0.wireOp",EDGE,"E4.0"),sQuery(id+"F0.wireOp",EDGE,"E4.1"),subQ1,subQ0])],"isStart":false})])],"derivedFrom":makeQuery(id+"F4.opExtrude","SWEPT_EDGE",EDGE,{"disambiguationData":[OSD([subQ3,subQ2])]})});}
            var Q1;
            Q1=makeQuery(id+"F4.opExtrude","SWEPT_EDGE",EDGE,{"disambiguationData":[OSD([sQuery(id+"F0.wireOp",EDGE,"E1.top"),sQuery(id+"F0.wireOp",EDGE,"E1.right")])]});
            var Q2;
            Q2=makeQuery(id+"F4.opExtrude","SWEPT_EDGE",EDGE,{"disambiguationData":[OSD([sQuery(id+"F0.wireOp",EDGE,"fd176c51-96d4-47cc-b5ac-51faa9285e0e.top"),sQuery(id+"F0.wireOp",EDGE,"fd176c51-96d4-47cc-b5ac-51faa9285e0e.left")])]});
            var Q3;
            Q3=makeQuery(id+"F4.opExtrude","SWEPT_EDGE",EDGE,{"disambiguationData":[OSD([sQuery(id+"F0.wireOp",EDGE,"E3.top"),sQuery(id+"F0.wireOp",EDGE,"E3.left")])]});
            var Q4;
            Q4=makeQuery(id+"F4.opExtrude","SWEPT_EDGE",EDGE,{"disambiguationData":[OSD([sQuery(id+"F0.wireOp",EDGE,"E1.bottom"),sQuery(id+"F0.wireOp",EDGE,"E1.right")])]});
            var Q5;
            Q5=makeQuery(id+"F4.opExtrude","SWEPT_EDGE",EDGE,{"disambiguationData":[OSD([sQuery(id+"F0.wireOp",EDGE,"fd176c51-96d4-47cc-b5ac-51faa9285e0e.top"),sQuery(id+"F0.wireOp",EDGE,"fd176c51-96d4-47cc-b5ac-51faa9285e0e.right")])]});
            var Q6;
            Q6=makeQuery(id+"F4.opExtrude","SWEPT_EDGE",EDGE,{"disambiguationData":[OSD([sQuery(id+"F0.wireOp",EDGE,"E3.bottom"),sQuery(id+"F0.wireOp",EDGE,"E3.right")])]});
            var Q7;
            Q7=makeQuery(id+"F4.opExtrude","SWEPT_EDGE",EDGE,{"disambiguationData":[OSD([sQuery(id+"F0.wireOp",EDGE,"E1.bottom"),sQuery(id+"F0.wireOp",EDGE,"E1.left")])]});
            var Q8;
            Q8=makeQuery(id+"F4.opExtrude","SWEPT_EDGE",EDGE,{"disambiguationData":[OSD([sQuery(id+"F0.wireOp",EDGE,"fd176c51-96d4-47cc-b5ac-51faa9285e0e.bottom"),sQuery(id+"F0.wireOp",EDGE,"fd176c51-96d4-47cc-b5ac-51faa9285e0e.right")])]});
            var Q9;
            Q9=makeQuery(id+"F4.opExtrude","SWEPT_EDGE",EDGE,{"disambiguationData":[OSD([sQuery(id+"F0.wireOp",EDGE,"E3.bottom"),sQuery(id+"F0.wireOp",EDGE,"E3.left")])]});
            var Q10;
            Q10=makeQuery(id+"F4.opExtrude","SWEPT_EDGE",EDGE,{"disambiguationData":[OSD([sQuery(id+"F0.wireOp",EDGE,"E1.top"),sQuery(id+"F0.wireOp",EDGE,"E1.left")])]});
            var Q11;
            Q11=makeQuery(id+"F1.opExtrude","SWEPT_EDGE",EDGE,{"disambiguationData":[OSD([sQuery(id+"F0.wireOp",EDGE,"3a2dc303-47aa-4c9f-8a0b-a45130b42c00.0"),sQuery(id+"F0.wireOp",EDGE,"3a2dc303-47aa-4c9f-8a0b-a45130b42c00.1")])]});
            var Q12;
            Q12=makeQuery(id+"F1.opExtrude","SWEPT_EDGE",EDGE,{"disambiguationData":[OSD([sQuery(id+"F0.wireOp",EDGE,"E7.0"),sQuery(id+"F0.wireOp",EDGE,"E7.1")])]});
            var Q13;
            Q13=makeQuery(id+"F1.opExtrude","SWEPT_EDGE",EDGE,{"disambiguationData":[OSD([sQuery(id+"F0.wireOp",EDGE,"E6.0"),sQuery(id+"F0.wireOp",EDGE,"E6.1")])]});
            var Q14;
            Q14=makeQuery(id+"F1.opExtrude","SWEPT_EDGE",EDGE,{"disambiguationData":[OSD([sQuery(id+"F0.wireOp",EDGE,"E6.0"),sQuery(id+"F0.wireOp",EDGE,"E6.3")])]});
            var Q15;
            Q15=makeQuery(id+"F1.opExtrude","SWEPT_EDGE",EDGE,{"disambiguationData":[OSD([sQuery(id+"F0.wireOp",EDGE,"E7.1"),sQuery(id+"F0.wireOp",EDGE,"E7.2")])]});
            var Q16;
            Q16=makeQuery(id+"F1.opExtrude","SWEPT_EDGE",EDGE,{"disambiguationData":[OSD([sQuery(id+"F0.wireOp",EDGE,"E6.2"),sQuery(id+"F0.wireOp",EDGE,"E6.3")])]});
            var Q17;
            Q17=makeQuery(id+"F1.opExtrude","SWEPT_EDGE",EDGE,{"disambiguationData":[OSD([sQuery(id+"F0.wireOp",EDGE,"E7.2"),sQuery(id+"F0.wireOp",EDGE,"E7.3")])]});
            var Q18;
            Q18=makeQuery(id+"F1.opExtrude","SWEPT_EDGE",EDGE,{"disambiguationData":[OSD([sQuery(id+"F0.wireOp",EDGE,"E6.1"),sQuery(id+"F0.wireOp",EDGE,"E6.2")])]});
            var Q19;
            Q19=makeQuery(id+"F1.opExtrude","SWEPT_EDGE",EDGE,{"disambiguationData":[OSD([sQuery(id+"F0.wireOp",EDGE,"E7.0"),sQuery(id+"F0.wireOp",EDGE,"E7.3")])]});
            var Q20;
            Q20=makeQuery(id+"F1.opExtrude","SWEPT_EDGE",EDGE,{"disambiguationData":[OSD([sQuery(id+"F0.wireOp",EDGE,"3a2dc303-47aa-4c9f-8a0b-a45130b42c00.0"),sQuery(id+"F0.wireOp",EDGE,"3a2dc303-47aa-4c9f-8a0b-a45130b42c00.3")])]});
            var Q21;
            Q21=makeQuery(id+"F1.opExtrude","SWEPT_EDGE",EDGE,{"disambiguationData":[OSD([sQuery(id+"F0.wireOp",EDGE,"3a2dc303-47aa-4c9f-8a0b-a45130b42c00.2"),sQuery(id+"F0.wireOp",EDGE,"3a2dc303-47aa-4c9f-8a0b-a45130b42c00.3")])]});
            var Q22;
            Q22=makeQuery(id+"F1.opExtrude","SWEPT_EDGE",EDGE,{"disambiguationData":[OSD([sQuery(id+"F0.wireOp",EDGE,"3a2dc303-47aa-4c9f-8a0b-a45130b42c00.1"),sQuery(id+"F0.wireOp",EDGE,"3a2dc303-47aa-4c9f-8a0b-a45130b42c00.2")])]});
            var Q23;
            Q23=makeQuery(id+"F4.opExtrude","SWEPT_EDGE",EDGE,{"disambiguationData":[OSD([sQuery(id+"F0.wireOp",EDGE,"fd176c51-96d4-47cc-b5ac-51faa9285e0e.bottom"),sQuery(id+"F0.wireOp",EDGE,"fd176c51-96d4-47cc-b5ac-51faa9285e0e.left")])]});
            var Q24;
            Q24=makeQuery(id+"F4.opExtrude","SWEPT_EDGE",EDGE,{"disambiguationData":[OSD([sQuery(id+"F0.wireOp",EDGE,"E10.0"),sQuery(id+"F0.wireOp",EDGE,"E10.1")])]});
            var Q25;
            Q25=makeQuery(id+"F4.opExtrude","SWEPT_EDGE",EDGE,{"disambiguationData":[OSD([sQuery(id+"F0.wireOp",EDGE,"E10.0"),sQuery(id+"F0.wireOp",EDGE,"E10.3")])]});
            var Q26;
            Q26=makeQuery(id+"F1.opExtrude","SWEPT_EDGE",EDGE,{"disambiguationData":[OSD([sQuery(id+"F0.wireOp",EDGE,"E11.0"),sQuery(id+"F0.wireOp",EDGE,"E11.3")])]});
            var Q27;
            Q27=makeQuery(id+"F1.opExtrude","SWEPT_EDGE",EDGE,{"disambiguationData":[OSD([sQuery(id+"F0.wireOp",EDGE,"E11.0"),sQuery(id+"F0.wireOp",EDGE,"E11.1")])]});
            var Q28;
            Q28=makeQuery(id+"F4.opExtrude","SWEPT_EDGE",EDGE,{"disambiguationData":[OSD([sQuery(id+"F0.wireOp",EDGE,"E10.1"),sQuery(id+"F0.wireOp",EDGE,"E10.2")])]});
            var Q29;
            Q29=makeQuery(id+"F1.opExtrude","SWEPT_EDGE",EDGE,{"disambiguationData":[OSD([sQuery(id+"F0.wireOp",EDGE,"E11.2"),sQuery(id+"F0.wireOp",EDGE,"E11.3")])]});
            var Q30;
            Q30=makeQuery(id+"F4.opExtrude","SWEPT_EDGE",EDGE,{"disambiguationData":[OSD([sQuery(id+"F0.wireOp",EDGE,"E10.2"),sQuery(id+"F0.wireOp",EDGE,"E10.3")])]});
            var Q31;
            Q31=makeQuery(id+"F1.opExtrude","SWEPT_EDGE",EDGE,{"disambiguationData":[OSD([sQuery(id+"F0.wireOp",EDGE,"E11.1"),sQuery(id+"F0.wireOp",EDGE,"E11.2")])]});
            fillet(context, id + "F25", {"entities" : qUnion([Q0, Q1, Q2, Q3, Q4, Q5, Q6, Q7, Q8, Q9, Q10, Q11, Q12, Q13, Q14, Q15, Q16, Q17, Q18, Q19, Q20, Q21, Q22, Q23, Q24, Q25, Q26, Q27, Q28, Q29, Q30, Q31]), "radius" : 3 * mm, "tangentPropagation" : true, "allowEdgeOverflow" : false});
        }
        {
            var Q0;
            Q0=makeQuery(id+"F8.boolean.opBoolean","COPY",EDGE,{"derivedFrom":makeQuery(id+"F8.opExtrude","CAP_EDGE",EDGE,{"disambiguationData":[OSD([sQuery(id+"F7.wireOp",EDGE,"E42")])],"isStart":false})});
            var Q1;
            Q1=makeQuery(id+"F9.boolean.opBoolean","COPY",EDGE,{"derivedFrom":makeQuery(id+"F9.opExtrude","CAP_EDGE",EDGE,{"disambiguationData":[OSD([sQuery(id+"F7.wireOp",EDGE,"E47")])],"isStart":false})});
            var Q2;
            Q2=makeQuery(id+"F9.boolean.opBoolean","COPY",EDGE,{"derivedFrom":makeQuery(id+"F9.opExtrude","CAP_EDGE",EDGE,{"disambiguationData":[OSD([sQuery(id+"F7.wireOp",EDGE,"E42")])],"isStart":false})});
            var Q3;
            Q3=makeQuery(id+"F8.boolean.opBoolean","COPY",EDGE,{"derivedFrom":makeQuery(id+"F8.opExtrude","CAP_EDGE",EDGE,{"disambiguationData":[OSD([sQuery(id+"F7.wireOp",EDGE,"E44")])],"isStart":false})});
            var Q4;
            Q4=makeQuery(id+"F8.boolean.opBoolean","COPY",EDGE,{"derivedFrom":makeQuery(id+"F8.opExtrude","CAP_EDGE",EDGE,{"disambiguationData":[OSD([sQuery(id+"F7.wireOp",EDGE,"E44")])],"isStart":true})});
            var Q5;
            Q5=makeQuery(id+"F9.boolean.opBoolean","COPY",EDGE,{"derivedFrom":makeQuery(id+"F9.opExtrude","CAP_EDGE",EDGE,{"disambiguationData":[OSD([sQuery(id+"F7.wireOp",EDGE,"E47")])],"isStart":true})});
            var Q6;
            Q6=makeQuery(id+"F8.boolean.opBoolean","COPY",EDGE,{"derivedFrom":makeQuery(id+"F8.opExtrude","CAP_EDGE",EDGE,{"disambiguationData":[OSD([sQuery(id+"F7.wireOp",EDGE,"E49")])],"isStart":false})});
            var Q7;
            Q7=makeQuery(id+"F8.boolean.opBoolean","COPY",EDGE,{"derivedFrom":makeQuery(id+"F8.opExtrude","CAP_EDGE",EDGE,{"disambiguationData":[OSD([sQuery(id+"F7.wireOp",EDGE,"E51")])],"isStart":false})});
            var Q8;
            Q8=makeQuery(id+"F8.boolean.opBoolean","COPY",EDGE,{"derivedFrom":makeQuery(id+"F8.opExtrude","CAP_EDGE",EDGE,{"disambiguationData":[OSD([sQuery(id+"F7.wireOp",EDGE,"E51")])],"isStart":true})});
            var Q9;
            Q9=makeQuery(id+"F8.boolean.opBoolean","COPY",EDGE,{"derivedFrom":makeQuery(id+"F8.opExtrude","CAP_EDGE",EDGE,{"disambiguationData":[OSD([sQuery(id+"F7.wireOp",EDGE,"E49")])],"isStart":true})});
            var Q10;
            Q10=makeQuery(id+"F8.boolean.opBoolean","COPY",EDGE,{"derivedFrom":makeQuery(id+"F8.opExtrude","CAP_EDGE",EDGE,{"disambiguationData":[OSD([sQuery(id+"F7.wireOp",EDGE,"E55")])],"isStart":false})});
            var Q11;
            Q11=makeQuery(id+"F8.boolean.opBoolean","COPY",EDGE,{"derivedFrom":makeQuery(id+"F8.opExtrude","CAP_EDGE",EDGE,{"disambiguationData":[OSD([sQuery(id+"F7.wireOp",EDGE,"E53")])],"isStart":false})});
            var Q12;
            Q12=makeQuery(id+"F8.boolean.opBoolean","COPY",EDGE,{"derivedFrom":makeQuery(id+"F8.opExtrude","CAP_EDGE",EDGE,{"disambiguationData":[OSD([sQuery(id+"F7.wireOp",EDGE,"E53")])],"isStart":true})});
            var Q13;
            Q13=makeQuery(id+"F8.boolean.opBoolean","COPY",EDGE,{"derivedFrom":makeQuery(id+"F8.opExtrude","CAP_EDGE",EDGE,{"disambiguationData":[OSD([sQuery(id+"F7.wireOp",EDGE,"E55")])],"isStart":true})});
            fillet(context, id + "F26", {"entities" : qUnion([Q0, Q1, Q2, Q3, Q4, Q5, Q6, Q7, Q8, Q9, Q10, Q11, Q12, Q13]), "radius" : 2 * mm, "tangentPropagation" : true, "allowEdgeOverflow" : false});
        }
        {
            var Q0;
            Q0=makeQuery(id+"F8.boolean.opBoolean","COPY",EDGE,{"derivedFrom":makeQuery(id+"F8.opExtrude","CAP_EDGE",EDGE,{"disambiguationData":[OSD([sQuery(id+"F5.wireOp",EDGE,"E25")])],"isStart":false})});
            var Q1;
            Q1=makeQuery(id+"F8.boolean.opBoolean","COPY",EDGE,{"derivedFrom":makeQuery(id+"F8.opExtrude","CAP_EDGE",EDGE,{"disambiguationData":[OSD([sQuery(id+"F5.wireOp",EDGE,"E23")])],"isStart":false})});
            var Q2;
            Q2=makeQuery(id+"F8.boolean.opBoolean","COPY",EDGE,{"derivedFrom":makeQuery(id+"F8.opExtrude","CAP_EDGE",EDGE,{"disambiguationData":[OSD([sQuery(id+"F5.wireOp",EDGE,"E25")])],"isStart":true})});
            var Q3;
            Q3=makeQuery(id+"F8.boolean.opBoolean","COPY",EDGE,{"derivedFrom":makeQuery(id+"F8.opExtrude","CAP_EDGE",EDGE,{"disambiguationData":[OSD([sQuery(id+"F5.wireOp",EDGE,"E23")])],"isStart":true})});
            var Q4;
            Q4=makeQuery(id+"F8.boolean.opBoolean","COPY",EDGE,{"derivedFrom":makeQuery(id+"F8.opExtrude","CAP_EDGE",EDGE,{"disambiguationData":[OSD([sQuery(id+"F5.wireOp",EDGE,"E19")])],"isStart":true})});
            var Q5;
            Q5=makeQuery(id+"F8.boolean.opBoolean","COPY",EDGE,{"derivedFrom":makeQuery(id+"F8.opExtrude","CAP_EDGE",EDGE,{"disambiguationData":[OSD([sQuery(id+"F5.wireOp",EDGE,"E21")])],"isStart":true})});
            var Q6;
            Q6=makeQuery(id+"F8.boolean.opBoolean","COPY",EDGE,{"derivedFrom":makeQuery(id+"F8.opExtrude","CAP_EDGE",EDGE,{"disambiguationData":[OSD([sQuery(id+"F5.wireOp",EDGE,"E21")])],"isStart":false})});
            var Q7;
            Q7=makeQuery(id+"F8.boolean.opBoolean","COPY",EDGE,{"derivedFrom":makeQuery(id+"F8.opExtrude","CAP_EDGE",EDGE,{"disambiguationData":[OSD([sQuery(id+"F5.wireOp",EDGE,"E19")])],"isStart":false})});
            var Q8;
            Q8=makeQuery(id+"F8.boolean.opBoolean","COPY",EDGE,{"derivedFrom":makeQuery(id+"F8.opExtrude","CAP_EDGE",EDGE,{"disambiguationData":[OSD([sQuery(id+"F5.wireOp",EDGE,"E14")])],"isStart":false})});
            var Q9;
            Q9=makeQuery(id+"F9.boolean.opBoolean","COPY",EDGE,{"derivedFrom":makeQuery(id+"F9.opExtrude","CAP_EDGE",EDGE,{"disambiguationData":[OSD([sQuery(id+"F5.wireOp",EDGE,"E17")])],"isStart":false})});
            var Q10;
            Q10=makeQuery(id+"F9.boolean.opBoolean","COPY",EDGE,{"derivedFrom":makeQuery(id+"F9.opExtrude","CAP_EDGE",EDGE,{"disambiguationData":[OSD([sQuery(id+"F5.wireOp",EDGE,"E14")])],"isStart":false})});
            var Q11;
            Q11=makeQuery(id+"F9.boolean.opBoolean","COPY",EDGE,{"derivedFrom":makeQuery(id+"F9.opExtrude","CAP_EDGE",EDGE,{"disambiguationData":[OSD([sQuery(id+"F5.wireOp",EDGE,"E17")])],"isStart":true})});
            var Q12;
            Q12=makeQuery(id+"F8.boolean.opBoolean","COPY",EDGE,{"derivedFrom":makeQuery(id+"F8.opExtrude","CAP_EDGE",EDGE,{"disambiguationData":[OSD([sQuery(id+"F5.wireOp",EDGE,"E12")])],"isStart":true})});
            var Q13;
            Q13=makeQuery(id+"F8.boolean.opBoolean","COPY",EDGE,{"derivedFrom":makeQuery(id+"F8.opExtrude","CAP_EDGE",EDGE,{"disambiguationData":[OSD([sQuery(id+"F5.wireOp",EDGE,"E12")])],"isStart":false})});
            fillet(context, id + "F27", {"entities" : qUnion([Q0, Q1, Q2, Q3, Q4, Q5, Q6, Q7, Q8, Q9, Q10, Q11, Q12, Q13]), "radius" : 2 * mm, "tangentPropagation" : true, "allowEdgeOverflow" : false});
        }
        {
            var Q0;
            Q0=makeQuery(id+"F8.boolean.opBoolean","COPY",EDGE,{"derivedFrom":makeQuery(id+"F8.opExtrude","CAP_EDGE",EDGE,{"disambiguationData":[OSD([sQuery(id+"F6.wireOp",EDGE,"E27")])],"isStart":false})});
            var Q1;
            Q1=makeQuery(id+"F8.boolean.opBoolean","COPY",EDGE,{"derivedFrom":makeQuery(id+"F8.opExtrude","CAP_EDGE",EDGE,{"disambiguationData":[OSD([sQuery(id+"F6.wireOp",EDGE,"E36")])],"isStart":false})});
            var Q2;
            Q2=makeQuery(id+"F8.boolean.opBoolean","COPY",EDGE,{"derivedFrom":makeQuery(id+"F8.opExtrude","CAP_EDGE",EDGE,{"disambiguationData":[OSD([sQuery(id+"F6.wireOp",EDGE,"E38")])],"isStart":false})});
            var Q3;
            Q3=makeQuery(id+"F9.boolean.opBoolean","COPY",EDGE,{"derivedFrom":makeQuery(id+"F9.opExtrude","CAP_EDGE",EDGE,{"disambiguationData":[OSD([sQuery(id+"F6.wireOp",EDGE,"E29")])],"isStart":false})});
            var Q4;
            Q4=makeQuery(id+"F9.boolean.opBoolean","COPY",EDGE,{"derivedFrom":makeQuery(id+"F9.opExtrude","CAP_EDGE",EDGE,{"disambiguationData":[OSD([sQuery(id+"F6.wireOp",EDGE,"E32")])],"isStart":false})});
            var Q5;
            Q5=makeQuery(id+"F9.boolean.opBoolean","COPY",EDGE,{"derivedFrom":makeQuery(id+"F9.opExtrude","CAP_EDGE",EDGE,{"disambiguationData":[OSD([sQuery(id+"F6.wireOp",EDGE,"E32")])],"isStart":true})});
            var Q6;
            Q6=makeQuery(id+"F8.boolean.opBoolean","COPY",EDGE,{"derivedFrom":makeQuery(id+"F8.opExtrude","CAP_EDGE",EDGE,{"disambiguationData":[OSD([sQuery(id+"F6.wireOp",EDGE,"E36")])],"isStart":true})});
            var Q7;
            Q7=makeQuery(id+"F8.boolean.opBoolean","COPY",EDGE,{"derivedFrom":makeQuery(id+"F8.opExtrude","CAP_EDGE",EDGE,{"disambiguationData":[OSD([sQuery(id+"F6.wireOp",EDGE,"E38")])],"isStart":true})});
            var Q8;
            Q8=makeQuery(id+"F8.boolean.opBoolean","COPY",EDGE,{"derivedFrom":makeQuery(id+"F8.opExtrude","CAP_EDGE",EDGE,{"disambiguationData":[OSD([sQuery(id+"F6.wireOp",EDGE,"E35")])],"isStart":true})});
            var Q9;
            Q9=makeQuery(id+"F8.boolean.opBoolean","COPY",EDGE,{"derivedFrom":makeQuery(id+"F8.opExtrude","CAP_EDGE",EDGE,{"disambiguationData":[OSD([sQuery(id+"F6.wireOp",EDGE,"E40")])],"isStart":true})});
            var Q10;
            Q10=makeQuery(id+"F8.boolean.opBoolean","COPY",EDGE,{"derivedFrom":makeQuery(id+"F8.opExtrude","CAP_EDGE",EDGE,{"disambiguationData":[OSD([sQuery(id+"F6.wireOp",EDGE,"E35")])],"isStart":false})});
            var Q11;
            Q11=makeQuery(id+"F8.boolean.opBoolean","COPY",EDGE,{"derivedFrom":makeQuery(id+"F8.opExtrude","CAP_EDGE",EDGE,{"disambiguationData":[OSD([sQuery(id+"F6.wireOp",EDGE,"E40")])],"isStart":false})});
            var Q12;
            Q12=makeQuery(id+"F8.boolean.opBoolean","COPY",EDGE,{"derivedFrom":makeQuery(id+"F8.opExtrude","CAP_EDGE",EDGE,{"disambiguationData":[OSD([sQuery(id+"F6.wireOp",EDGE,"E27")])],"isStart":true})});
            var Q13;
            Q13=makeQuery(id+"F8.boolean.opBoolean","COPY",EDGE,{"derivedFrom":makeQuery(id+"F8.opExtrude","CAP_EDGE",EDGE,{"disambiguationData":[OSD([sQuery(id+"F6.wireOp",EDGE,"E29")])],"isStart":false})});
            fillet(context, id + "F28", {"entities" : qUnion([Q0, Q1, Q2, Q3, Q4, Q5, Q6, Q7, Q8, Q9, Q10, Q11, Q12, Q13]), "radius" : 2 * mm, "tangentPropagation" : true, "allowEdgeOverflow" : false});
        }
        {
            var Q0;
            Q0=makeQuery(id+"F1.opExtrude","SWEPT_EDGE",EDGE,{"disambiguationData":[OSD([sQuery(id+"F0.wireOp",EDGE,"E2.1"),sQuery(id+"F0.wireOp",EDGE,"E2.2"),sQuery(id+"F0.wireOp",EDGE,"E4.3")])]});
            var Q1;
            Q1=makeQuery(id+"F1.opExtrude","SWEPT_EDGE",EDGE,{"disambiguationData":[OSD([sQuery(id+"F0.wireOp",EDGE,"E2.1"),sQuery(id+"F0.wireOp",EDGE,"E5.1"),sQuery(id+"F0.wireOp",EDGE,"E5.2")])]});
            var Q2;
            Q2=makeQuery(id+"F1.opExtrude","SWEPT_EDGE",EDGE,{"disambiguationData":[OSD([sQuery(id+"F0.wireOp",EDGE,"E4.0"),sQuery(id+"F0.wireOp",EDGE,"E4.3"),sQuery(id+"F0.wireOp",EDGE,"E5.1")])]});
            fillet(context, id + "F29", {"entities" : qUnion([Q0, Q1, Q2]), "radius" : 12 * mm, "tangentPropagation" : true, "allowEdgeOverflow" : false});
        }
    });
